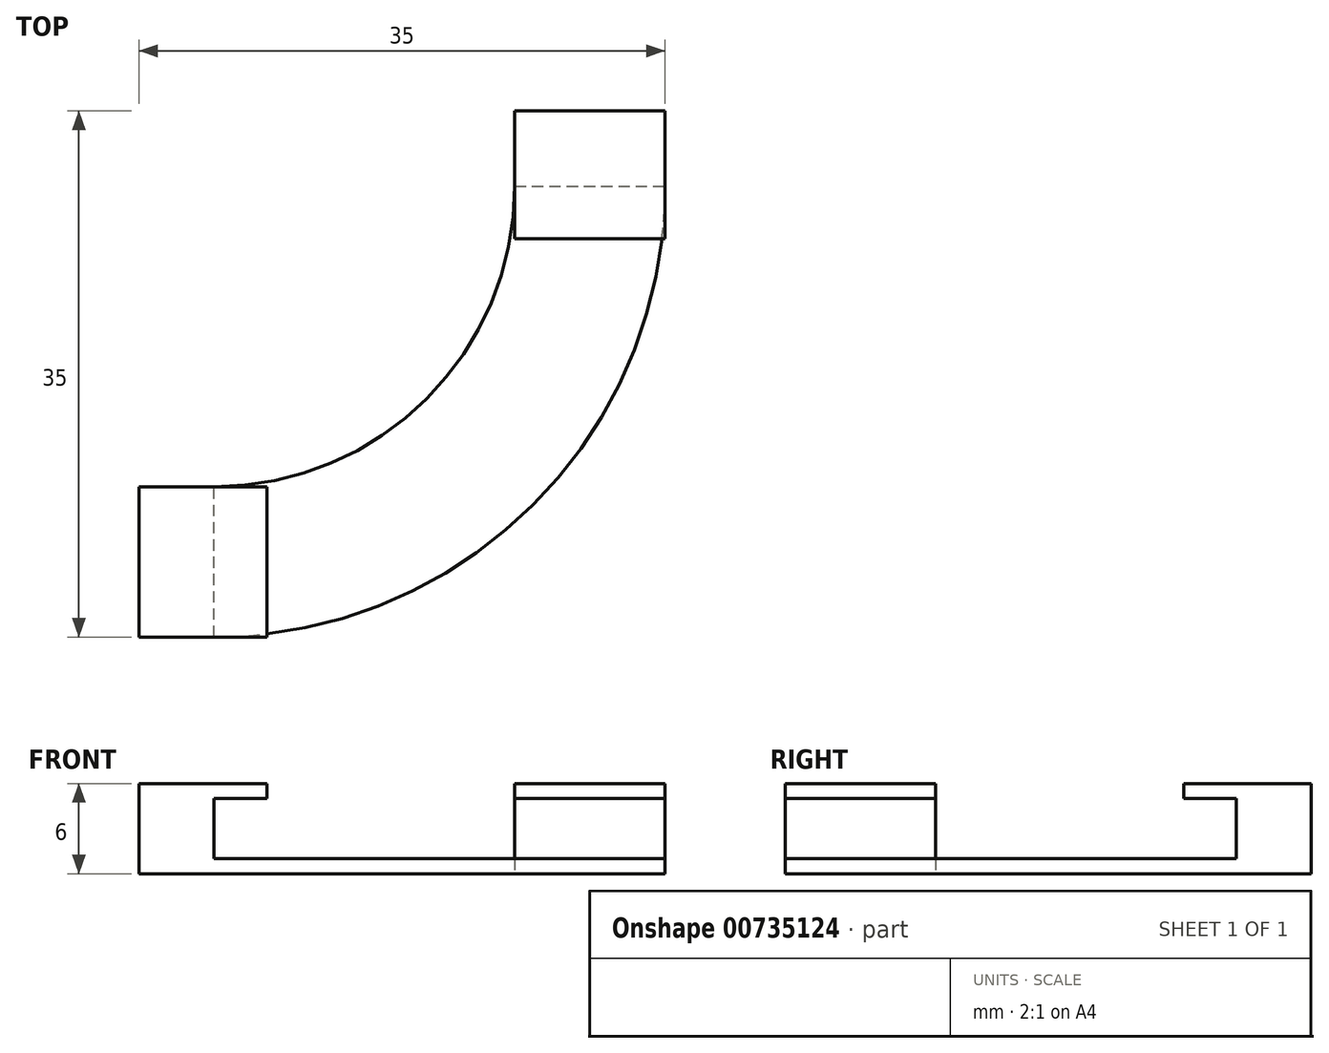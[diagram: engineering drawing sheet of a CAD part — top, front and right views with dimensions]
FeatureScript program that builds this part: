
annotation { "Feature Type Name" : "Feature", "Feature Type Description" : "" }
export const myFeature = defineFeature(function(context is Context, id is Id, definition is map)
    precondition{}
    {
        {
            var Q0;
            Q0=qCreatedBy(makeId("Top.planeOp"),FACE);
            var sketch = newSketch(context, id + "F0", { "sketchPlane" : qUnion([Q0])});
            skCircle(sketch, "E0", {"center": v(0, 0) * mm, "radius": 20 * mm});
            skCircle(sketch, "E1", {"center": v(0, 0) * mm, "radius": 30 * mm});
            skLineSegment(sketch, "E2", {"start": v(0, 0) * mm, "end": v(0, -30) * mm});
            skLineSegment(sketch, "E3", {"start": v(-0.47, 0) * mm, "end": v(30, 0) * mm});
            skLineSegment(sketch, "E4.left", {"start": v(0, -20) * mm, "end": v(0, -25) * mm});
            skLineSegment(sketch, "E5", {"start": v(30, 0) * mm, "end": v(30, 5) * mm});
            skLineSegment(sketch, "E6", {"start": v(30, 5) * mm, "end": v(20, 5) * mm});
            skLineSegment(sketch, "E7", {"start": v(20, 5) * mm, "end": v(20, 0) * mm});
            skLineSegment(sketch, "E8", {"start": v(0, -20) * mm, "end": v(-5, -20) * mm});
            skLineSegment(sketch, "E9", {"start": v(-5, -20) * mm, "end": v(-5, -30) * mm});
            skLineSegment(sketch, "E10", {"start": v(-5, -30) * mm, "end": v(0, -30) * mm});
            skSolve(sketch);
        }
        {
            var Q0;
            {var subQ5=sQuery(id+"F0.wireOp",EDGE,"E7");Q0=makeQuery(id+"F0.imprint","IMPRINT",FACE,{"disambiguationData":[TD([[makeQuery(id+"F0.imprint","IMPRINT",EDGE,{"derivedFrom":subQ5}),1.0]])]});}
            var Q1;
            {var subQ0=sQuery(id+"F0.wireOp",EDGE,"E5");Q1=makeQuery(id+"F0.imprint","IMPRINT",FACE,{"disambiguationData":[TD([[makeQuery(id+"F0.imprint","IMPRINT",EDGE,{"derivedFrom":subQ0}),1.0]])]});}
            var Q2;
            {var subQ0=sQuery(id+"F0.wireOp",EDGE,"E2");var subQ3=makeQuery(id+"F0.imprint","IMPRINT",VERTEX,{"derivedFrom":subQ0});Q2=makeQuery(id+"F0.imprint","IMPRINT",FACE,{"disambiguationData":[TD([[makeQuery(id+"F0.imprint","IMPRINT",EDGE,{"disambiguationData":[TD([[subQ3,1.0]])],"derivedFrom":subQ0}),1.0]])]});}
            var Q3;
            {var subQ0=sQuery(id+"F0.wireOp",EDGE,"E8");Q3=makeQuery(id+"F0.imprint","IMPRINT",FACE,{"disambiguationData":[TD([[makeQuery(id+"F0.imprint","IMPRINT",EDGE,{"derivedFrom":subQ0}),1.0]])]});}
            var Q4;
            {var subQ0=sQuery(id+"F0.wireOp",EDGE,"E10");Q4=makeQuery(id+"F0.imprint","IMPRINT",FACE,{"disambiguationData":[TD([[makeQuery(id+"F0.imprint","IMPRINT",EDGE,{"derivedFrom":subQ0}),1.0]])]});}
            extrude(context, id + "F1", {"entities" : qUnion([Q0, Q1, Q2, Q3, Q4]), "depth" : 1 * mm, "offsetDistance" : 25 * mm});
        }
        {
            var Q0;
            Q0=makeQuery(id+"F1.opExtrude","CAP_FACE",FACE,{"disambiguationData":[OSD([sQuery(id+"F0.wireOp",EDGE,"E0"),sQuery(id+"F0.wireOp",EDGE,"E1"),sQuery(id+"F0.wireOp",EDGE,"E5"),sQuery(id+"F0.wireOp",EDGE,"E6"),sQuery(id+"F0.wireOp",EDGE,"E7"),sQuery(id+"F0.wireOp",EDGE,"E8"),sQuery(id+"F0.wireOp",EDGE,"E9"),sQuery(id+"F0.wireOp",EDGE,"E10")])],"isStart":false});
            var sketch = newSketch(context, id + "F2", { "sketchPlane" : qUnion([Q0])});
            skLineSegment(sketch, "E11", {"start": v(0, -30) * mm, "end": v(0, -20) * mm});
            skLineSegment(sketch, "E12", {"start": v(20, 0) * mm, "end": v(30, 0) * mm});
            skSolve(sketch);
        }
        {
            var Q0;
            Q0=makeQuery(id+"F2.imprint","IMPRINT",FACE,{"disambiguationData":[TD([[makeQuery(id+"F2.imprint","IMPRINT",EDGE,{"derivedFrom":sQuery(id+"F2.wireOp",EDGE,"E12")}),1.0]])]});
            var Q1;
            Q1=makeQuery(id+"F2.imprint","IMPRINT",FACE,{"disambiguationData":[TD([[makeQuery(id+"F2.imprint","IMPRINT",EDGE,{"derivedFrom":sQuery(id+"F2.wireOp",EDGE,"E11")}),1.0]])]});
            extrude(context, id + "F3", {"entities" : qUnion([Q0, Q1]), "operationType" : NewBodyOperationType.ADD, "depth" : 5 * mm, "offsetDistance" : 25 * mm});
        }
        {
            var Q0;
            Q0=makeQuery(id+"F3.opExtrude","SWEPT_FACE",FACE,{"disambiguationData":[OSD([sQuery(id+"F2.wireOp",EDGE,"E12")])]});
            var sketch = newSketch(context, id + "F4", { "sketchPlane" : qUnion([Q0])});
            skLineSegment(sketch, "E13", {"start": v(20, 5) * mm, "end": v(30, 5) * mm});
            skSolve(sketch);
        }
        {
            var Q0;
            Q0=makeQuery(id+"F3.opExtrude","SWEPT_FACE",FACE,{"disambiguationData":[OSD([sQuery(id+"F2.wireOp",EDGE,"E11")])]});
            var sketch = newSketch(context, id + "F5", { "sketchPlane" : qUnion([Q0])});
            skLineSegment(sketch, "E14", {"start": v(-30, 5) * mm, "end": v(-20, 5) * mm});
            skSolve(sketch);
        }
        {
            var Q0;
            {var subQ0=sQuery(id+"F5.wireOp",EDGE,"E14");Q0=makeQuery(id+"F5.imprint","IMPRINT",FACE,{"disambiguationData":[TD([[makeQuery(id+"F5.imprint","IMPRINT",EDGE,{"derivedFrom":subQ0}),1.0]])]});}
            extrude(context, id + "F6", {"entities" : qUnion([Q0]), "operationType" : NewBodyOperationType.ADD, "depth" : 3.5 * mm, "offsetDistance" : 25 * mm});
        }
        {
            var Q0;
            {var subQ0=sQuery(id+"F4.wireOp",EDGE,"E13");Q0=makeQuery(id+"F4.imprint","IMPRINT",FACE,{"disambiguationData":[TD([[makeQuery(id+"F4.imprint","IMPRINT",EDGE,{"derivedFrom":subQ0}),1.0]])]});}
            extrude(context, id + "F7", {"entities" : qUnion([Q0]), "operationType" : NewBodyOperationType.ADD, "depth" : 3.5 * mm, "offsetDistance" : 25 * mm});
        }
    });
